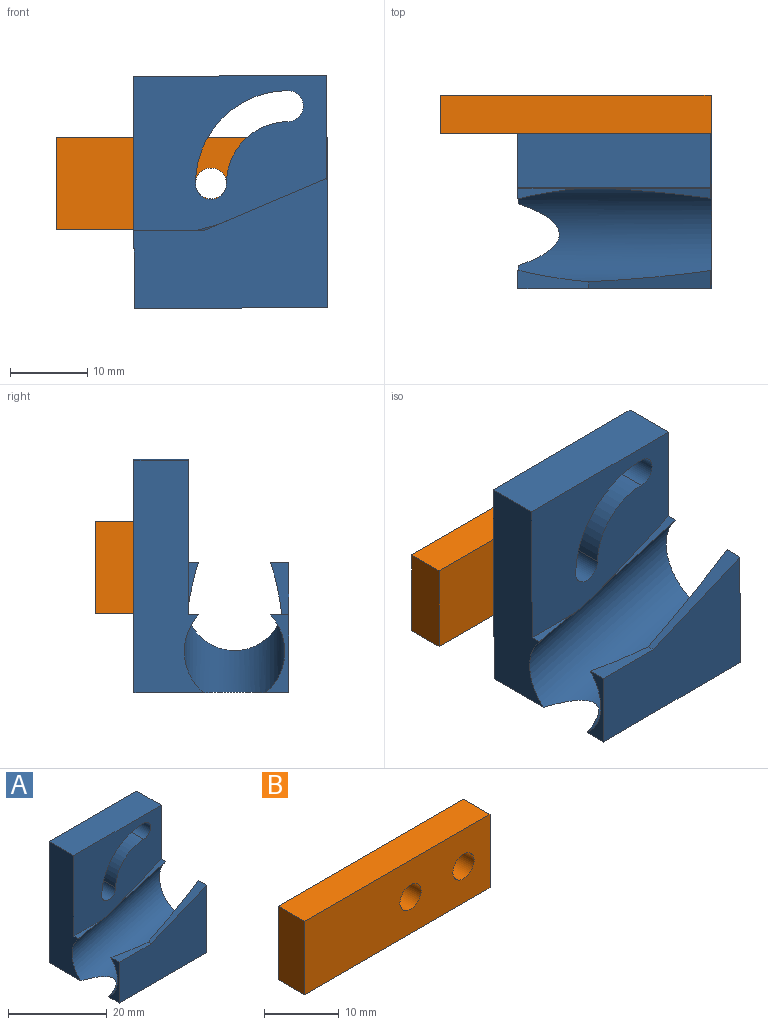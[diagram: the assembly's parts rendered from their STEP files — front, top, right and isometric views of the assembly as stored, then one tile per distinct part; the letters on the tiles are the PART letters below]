
ASSEMBLY  parts=2 mates=1
PART A: 19 faces, bbox 30.4x20x31.3 mm
  f0: plane 25x7mm, normal (0,0,1), area 175mm2, adj f2,f6,f7,f10
  f1: plane 25x16.69mm, normal (0,-1,0), area 304.1mm2, adj f4,f5,f6,f13,f14
  f2: plane 30.01x9.01mm, normal (-1,0,0), area 211.9mm2, adj f0,f3,f5,f7,f10,f11
  f3: cylinder r=6.5mm len=30.37mm, axis (0.97,0,0.26), area 683.6mm2, adj f2,f4,f5,f6,f10,f11,f12,f13
  f4: plane 10.06x3.01mm, normal (-1,0,0), area 11.9mm2, adj f1,f3,f5,f14
  f5: plane 25x20mm, normal (0,0,-1), area 471.2mm2, adj f1,f2,f3,f4,f6,f7
  f6: plane 30.01x20mm, normal (1,0,0), area 302.8mm2, adj f0,f1,f3,f5,f7,f10,f12,f13
  f7: plane 30.01x25mm, normal (0,1,0), area 659.6mm2, adj f0,f2,f5,f6,f8,f15,f16,f17
  f8: cylinder r=2.2mm len=5mm, axis (0,1,0), area 69.1mm2, adj f7,f9
  f9: plane 4.4x4.4mm, normal (0,1,0), area 15.2mm2, adj f8
  f10: plane 25x19.95mm, normal (0,-1,0), area 370.3mm2, adj f0,f2,f3,f6,f11,f12,f15,f16
  f11: plane 8.07x1.4mm, normal (0,0,1), area 4.8mm2, adj f2,f3,f10
  f12: plane 13.94x5.83mm, normal (-0.39,0,0.92), area 8.7mm2, adj f3,f6,f10
  f13: plane 15.85x6.63mm, normal (-0.39,0,0.92), area 25.7mm2, adj f1,f3,f6,f14
  f14: plane 9.15x2.4mm, normal (0,0,1), area 13.9mm2, adj f1,f3,f4,f13
  f15: cylinder r=2mm len=7mm, axis (0,1,0), area 44mm2, adj f7,f10,f16,f18
  f16: cylinder r=8mm len=8mm, axis (0,1,0), area 88mm2, adj f7,f10,f15,f17
  f17: cylinder r=2mm len=7mm, axis (0,1,0), area 44mm2, adj f7,f10,f16,f18
  f18: cylinder r=12mm len=12mm, axis (0,1,0), area 131.9mm2, adj f7,f10,f15,f17
PART B: 8 faces, bbox 35x5x12 mm
  f0: plane 12x5mm, normal (-1,0,0), area 60mm2, adj f1,f4,f6,f7
  f1: plane 35x5mm, normal (0,0,-1), area 175mm2, adj f0,f2,f6,f7
  f2: plane 12x5mm, normal (1,0,0), area 60mm2, adj f1,f4,f6,f7
  f3: cylinder r=2mm len=5mm, axis (0,1,0), area 62.8mm2, adj f6,f7
  f4: plane 35x5mm, normal (0,0,1), area 175mm2, adj f0,f2,f6,f7
  f5: cylinder r=2mm len=5mm, axis (0,1,0), area 62.8mm2, adj f6,f7
  f6: plane 35x12mm, normal (0,-1,0), area 394.9mm2, adj f0,f1,f2,f3,f4,f5
  f7: plane 35x12mm, normal (0,1,0), area 394.9mm2, adj f0,f1,f2,f3,f4,f5
PLACE A rot(axis=(0,-1,0),0.3deg) t=(10.03,0,-0.11)mm
PLACE B t=(0,5,0)mm
MATE revolute A.f8 <-> B.f3  axis (0,1,0) through (30,0,6)mm
